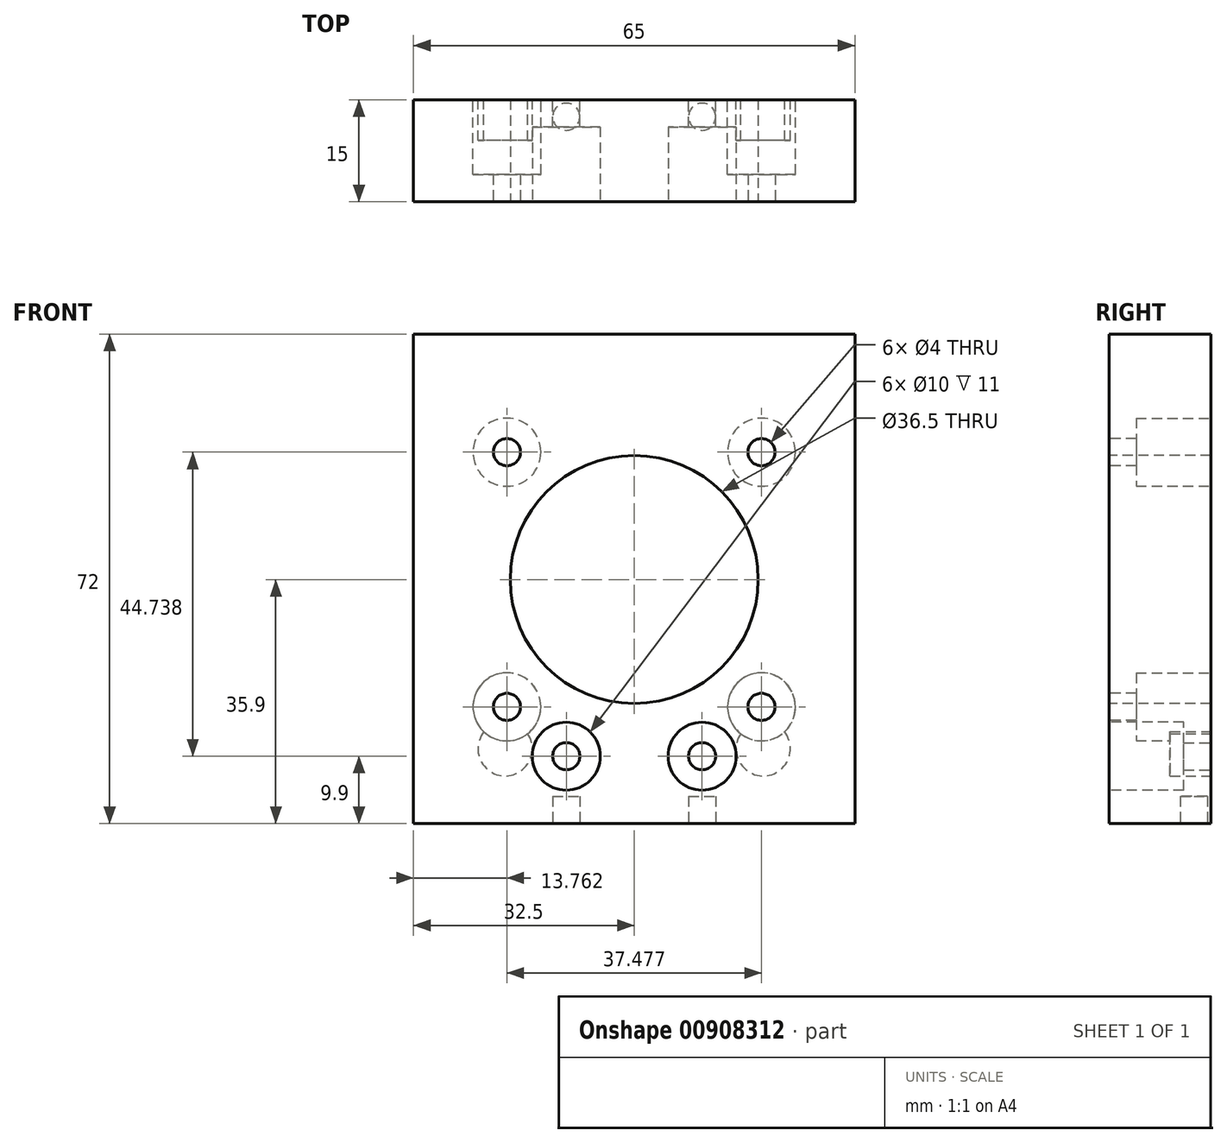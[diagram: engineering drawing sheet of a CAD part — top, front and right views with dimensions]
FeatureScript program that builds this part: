
annotation { "Feature Type Name" : "Feature", "Feature Type Description" : "" }
export const myFeature = defineFeature(function(context is Context, id is Id, definition is map)
    precondition{}
    {
        {
            var Q0;
            Q0=qCreatedBy(makeId("Front.planeOp"),FACE);
            var sketch = newSketch(context, id + "F0", { "sketchPlane" : qUnion([Q0])});
            skLineSegment(sketch, "E0.bottom", {"start": v(32.5, -32.5) * mm, "end": v(-32.5, -32.5) * mm});
            skLineSegment(sketch, "E0.top", {"start": v(32.5, 32.5) * mm, "end": v(-32.5, 32.5) * mm});
            skLineSegment(sketch, "E0.left", {"start": v(32.5, -32.5) * mm, "end": v(32.5, 32.5) * mm});
            skLineSegment(sketch, "E0.right", {"start": v(-32.5, -32.5) * mm, "end": v(-32.5, 32.5) * mm});
            skPoint(sketch, "E0.middle", {"position": v(0, 0) * mm});
            skSolve(sketch);
        }
        {
            var Q0;
            Q0 = qSketchRegion(id + "F0", true);
            extrude(context, id + "F1", {"entities" : qUnion([Q0]), "depth" : 15 * mm, "offsetDistance" : 25 * mm});
        }
        {
            var Q0;
            Q0=makeQuery(id+"F1.opExtrude","CAP_FACE",FACE,{"disambiguationData":[OSD([sQuery(id+"F0.wireOp",EDGE,"E0.bottom"),sQuery(id+"F0.wireOp",EDGE,"E0.top"),sQuery(id+"F0.wireOp",EDGE,"E0.left"),sQuery(id+"F0.wireOp",EDGE,"E0.right")])],"isStart":false});
            var sketch = newSketch(context, id + "F2", { "sketchPlane" : qUnion([Q0])});
            skLineSegment(sketch, "E1", {"start": v(0, -32.5) * mm, "end": v(0, 3.4) * mm});
            skCircle(sketch, "E2", {"center": v(0, 3.4) * mm, "radius": 18.25 * mm});
            skSolve(sketch);
        }
        {
            var Q0;
            Q0=makeQuery(id+"F2.imprint","IMPRINT",FACE,{"disambiguationData":[TD([[makeQuery(id+"F2.imprint","IMPRINT",EDGE,{"derivedFrom":sQuery(id+"F2.wireOp",EDGE,"E2")}),1.0]])]});
            extrude(context, id + "F3", {"entities" : qUnion([Q0]), "operationType" : NewBodyOperationType.REMOVE, "oppositeDirection" : true, "depth" : 15 * mm, "offsetDistance" : 25 * mm});
        }
        {
            var Q0;
            Q0=makeQuery(id+"F1.opExtrude","CAP_FACE",FACE,{"disambiguationData":[OSD([sQuery(id+"F0.wireOp",EDGE,"E0.bottom"),sQuery(id+"F0.wireOp",EDGE,"E0.top"),sQuery(id+"F0.wireOp",EDGE,"E0.left"),sQuery(id+"F0.wireOp",EDGE,"E0.right")])],"isStart":false});
            var sketch = newSketch(context, id + "F4", { "sketchPlane" : qUnion([Q0])});
            skCircle(sketch, "E3", {"center": v(0, 3.4) * mm, "radius": 26.5 * mm});
            skLineSegment(sketch, "E4.bottom", {"start": v(26.5, -23.1) * mm, "end": v(-26.5, -23.1) * mm});
            skLineSegment(sketch, "E4.top", {"start": v(26.5, 29.9) * mm, "end": v(-26.5, 29.9) * mm});
            skLineSegment(sketch, "E4.left", {"start": v(26.5, -23.1) * mm, "end": v(26.5, 29.9) * mm});
            skLineSegment(sketch, "E4.right", {"start": v(-26.5, -23.1) * mm, "end": v(-26.5, 29.9) * mm});
            skLineSegment(sketch, "E5", {"start": v(26.5, 29.9) * mm, "end": v(-26.5, -23.1) * mm});
            skLineSegment(sketch, "E6", {"start": v(26.5, -23.1) * mm, "end": v(-26.5, 29.9) * mm});
            skCircle(sketch, "E7", {"center": v(-18.74, 22.14) * mm, "radius": 2 * mm});
            skCircle(sketch, "E8", {"center": v(18.74, 22.14) * mm, "radius": 2 * mm});
            skCircle(sketch, "E9", {"center": v(-18.74, -15.34) * mm, "radius": 2 * mm});
            skCircle(sketch, "E10", {"center": v(18.74, -15.34) * mm, "radius": 2 * mm});
            skSolve(sketch);
        }
        {
            var Q0;
            {var subQ0=sQuery(id+"F4.wireOp",EDGE,"E6");var subQ1=sQuery(id+"F4.wireOp",EDGE,"E3");var subQ2=makeQuery(id+"F4.imprint","INTERSECT",VERTEX,{"disambiguationData":[OD(0.0)],"derivedFrom":[subQ1,subQ0]});Q0=makeQuery(id+"F4.imprint","IMPRINT",FACE,{"disambiguationData":[TD([[makeQuery(id+"F4.imprint","IMPRINT",EDGE,{"disambiguationData":[TD([[subQ2,-1.0]])],"derivedFrom":subQ1}),-1.0]])]});}
            var Q1;
            {var subQ0=sQuery(id+"F4.wireOp",EDGE,"E8");var subQ1=sQuery(id+"F4.wireOp",EDGE,"E3");var subQ2=makeQuery(id+"F4.imprint","INTERSECT",VERTEX,{"disambiguationData":[OD(0.0)],"derivedFrom":[subQ1,subQ0]});Q1=makeQuery(id+"F4.imprint","IMPRINT",FACE,{"disambiguationData":[TD([[makeQuery(id+"F4.imprint","IMPRINT",EDGE,{"disambiguationData":[TD([[subQ2,-1.0]])],"derivedFrom":subQ1}),-1.0]])]});}
            var Q2;
            {var subQ0=sQuery(id+"F4.wireOp",EDGE,"E5");var subQ1=sQuery(id+"F4.wireOp",EDGE,"E3");var subQ2=makeQuery(id+"F4.imprint","INTERSECT",VERTEX,{"disambiguationData":[OD(0.0)],"derivedFrom":[subQ1,subQ0]});Q2=makeQuery(id+"F4.imprint","IMPRINT",FACE,{"disambiguationData":[TD([[makeQuery(id+"F4.imprint","IMPRINT",EDGE,{"disambiguationData":[TD([[subQ2,-1.0]])],"derivedFrom":subQ1}),1.0]])]});}
            var Q3;
            {var subQ0=sQuery(id+"F4.wireOp",EDGE,"E5");var subQ1=sQuery(id+"F4.wireOp",EDGE,"E3");var subQ2=makeQuery(id+"F4.imprint","INTERSECT",VERTEX,{"disambiguationData":[OD(0.0)],"derivedFrom":[subQ1,subQ0]});Q3=makeQuery(id+"F4.imprint","IMPRINT",FACE,{"disambiguationData":[TD([[makeQuery(id+"F4.imprint","IMPRINT",EDGE,{"disambiguationData":[TD([[subQ2,-1.0]])],"derivedFrom":subQ1}),-1.0]])]});}
            var Q4;
            {var subQ0=sQuery(id+"F4.wireOp",EDGE,"E8");var subQ1=sQuery(id+"F4.wireOp",EDGE,"E3");var subQ2=makeQuery(id+"F4.imprint","INTERSECT",VERTEX,{"disambiguationData":[OD(0.0)],"derivedFrom":[subQ1,subQ0]});Q4=makeQuery(id+"F4.imprint","IMPRINT",FACE,{"disambiguationData":[TD([[makeQuery(id+"F4.imprint","IMPRINT",EDGE,{"disambiguationData":[TD([[subQ2,-1.0]])],"derivedFrom":subQ1}),1.0]])]});}
            var Q5;
            {var subQ0=sQuery(id+"F4.wireOp",EDGE,"E6");var subQ1=sQuery(id+"F4.wireOp",EDGE,"E3");var subQ2=makeQuery(id+"F4.imprint","INTERSECT",VERTEX,{"disambiguationData":[OD(1.0)],"derivedFrom":[subQ1,subQ0]});Q5=makeQuery(id+"F4.imprint","IMPRINT",FACE,{"disambiguationData":[TD([[makeQuery(id+"F4.imprint","IMPRINT",EDGE,{"disambiguationData":[TD([[subQ2,-1.0]])],"derivedFrom":subQ1}),-1.0]])]});}
            var Q6;
            {var subQ0=sQuery(id+"F4.wireOp",EDGE,"E6");var subQ1=sQuery(id+"F4.wireOp",EDGE,"E3");var subQ2=makeQuery(id+"F4.imprint","INTERSECT",VERTEX,{"disambiguationData":[OD(1.0)],"derivedFrom":[subQ1,subQ0]});Q6=makeQuery(id+"F4.imprint","IMPRINT",FACE,{"disambiguationData":[TD([[makeQuery(id+"F4.imprint","IMPRINT",EDGE,{"disambiguationData":[TD([[subQ2,-1.0]])],"derivedFrom":subQ1}),1.0]])]});}
            var Q7;
            {var subQ0=sQuery(id+"F4.wireOp",EDGE,"E10");var subQ1=sQuery(id+"F4.wireOp",EDGE,"E3");var subQ2=makeQuery(id+"F4.imprint","INTERSECT",VERTEX,{"disambiguationData":[OD(0.0)],"derivedFrom":[subQ1,subQ0]});Q7=makeQuery(id+"F4.imprint","IMPRINT",FACE,{"disambiguationData":[TD([[makeQuery(id+"F4.imprint","IMPRINT",EDGE,{"disambiguationData":[TD([[subQ2,-1.0]])],"derivedFrom":subQ1}),-1.0]])]});}
            var Q8;
            {var subQ0=sQuery(id+"F4.wireOp",EDGE,"E10");var subQ1=sQuery(id+"F4.wireOp",EDGE,"E3");var subQ2=makeQuery(id+"F4.imprint","INTERSECT",VERTEX,{"disambiguationData":[OD(0.0)],"derivedFrom":[subQ1,subQ0]});Q8=makeQuery(id+"F4.imprint","IMPRINT",FACE,{"disambiguationData":[TD([[makeQuery(id+"F4.imprint","IMPRINT",EDGE,{"disambiguationData":[TD([[subQ2,-1.0]])],"derivedFrom":subQ1}),1.0]])]});}
            var Q9;
            {var subQ0=sQuery(id+"F4.wireOp",EDGE,"E7");var subQ1=sQuery(id+"F4.wireOp",EDGE,"E3");var subQ2=makeQuery(id+"F4.imprint","INTERSECT",VERTEX,{"disambiguationData":[OD(0.0)],"derivedFrom":[subQ1,subQ0]});Q9=makeQuery(id+"F4.imprint","IMPRINT",FACE,{"disambiguationData":[TD([[makeQuery(id+"F4.imprint","IMPRINT",EDGE,{"disambiguationData":[TD([[subQ2,-1.0]])],"derivedFrom":subQ1}),-1.0]])]});}
            var Q10;
            {var subQ0=sQuery(id+"F4.wireOp",EDGE,"E7");var subQ1=sQuery(id+"F4.wireOp",EDGE,"E3");var subQ2=makeQuery(id+"F4.imprint","INTERSECT",VERTEX,{"disambiguationData":[OD(0.0)],"derivedFrom":[subQ1,subQ0]});Q10=makeQuery(id+"F4.imprint","IMPRINT",FACE,{"disambiguationData":[TD([[makeQuery(id+"F4.imprint","IMPRINT",EDGE,{"disambiguationData":[TD([[subQ2,-1.0]])],"derivedFrom":subQ1}),1.0]])]});}
            var Q11;
            {var subQ0=sQuery(id+"F4.wireOp",EDGE,"E6");var subQ1=sQuery(id+"F4.wireOp",EDGE,"E3");var subQ2=makeQuery(id+"F4.imprint","INTERSECT",VERTEX,{"disambiguationData":[OD(0.0)],"derivedFrom":[subQ1,subQ0]});Q11=makeQuery(id+"F4.imprint","IMPRINT",FACE,{"disambiguationData":[TD([[makeQuery(id+"F4.imprint","IMPRINT",EDGE,{"disambiguationData":[TD([[subQ2,-1.0]])],"derivedFrom":subQ1}),1.0]])]});}
            var Q12;
            {var subQ0=sQuery(id+"F4.wireOp",EDGE,"E5");var subQ1=sQuery(id+"F4.wireOp",EDGE,"E3");var subQ2=makeQuery(id+"F4.imprint","INTERSECT",VERTEX,{"disambiguationData":[OD(1.0)],"derivedFrom":[subQ1,subQ0]});Q12=makeQuery(id+"F4.imprint","IMPRINT",FACE,{"disambiguationData":[TD([[makeQuery(id+"F4.imprint","IMPRINT",EDGE,{"disambiguationData":[TD([[subQ2,-1.0]])],"derivedFrom":subQ1}),1.0]])]});}
            var Q13;
            {var subQ0=sQuery(id+"F4.wireOp",EDGE,"E9");var subQ1=sQuery(id+"F4.wireOp",EDGE,"E3");var subQ2=makeQuery(id+"F4.imprint","INTERSECT",VERTEX,{"disambiguationData":[OD(0.0)],"derivedFrom":[subQ1,subQ0]});Q13=makeQuery(id+"F4.imprint","IMPRINT",FACE,{"disambiguationData":[TD([[makeQuery(id+"F4.imprint","IMPRINT",EDGE,{"disambiguationData":[TD([[subQ2,-1.0]])],"derivedFrom":subQ1}),-1.0]])]});}
            var Q14;
            {var subQ0=sQuery(id+"F4.wireOp",EDGE,"E5");var subQ1=sQuery(id+"F4.wireOp",EDGE,"E3");var subQ2=makeQuery(id+"F4.imprint","INTERSECT",VERTEX,{"disambiguationData":[OD(1.0)],"derivedFrom":[subQ1,subQ0]});Q14=makeQuery(id+"F4.imprint","IMPRINT",FACE,{"disambiguationData":[TD([[makeQuery(id+"F4.imprint","IMPRINT",EDGE,{"disambiguationData":[TD([[subQ2,-1.0]])],"derivedFrom":subQ1}),-1.0]])]});}
            var Q15;
            {var subQ0=sQuery(id+"F4.wireOp",EDGE,"E9");var subQ1=sQuery(id+"F4.wireOp",EDGE,"E3");var subQ2=makeQuery(id+"F4.imprint","INTERSECT",VERTEX,{"disambiguationData":[OD(0.0)],"derivedFrom":[subQ1,subQ0]});Q15=makeQuery(id+"F4.imprint","IMPRINT",FACE,{"disambiguationData":[TD([[makeQuery(id+"F4.imprint","IMPRINT",EDGE,{"disambiguationData":[TD([[subQ2,-1.0]])],"derivedFrom":subQ1}),1.0]])]});}
            extrude(context, id + "F5", {"entities" : qUnion([Q0, Q1, Q2, Q3, Q4, Q5, Q6, Q7, Q8, Q9, Q10, Q11, Q12, Q13, Q14, Q15]), "operationType" : NewBodyOperationType.REMOVE, "oppositeDirection" : true, "depth" : 25 * mm, "offsetDistance" : 25 * mm});
        }
        {
            var Q0;
            Q0=makeQuery(id+"F1.opExtrude","CAP_FACE",FACE,{"disambiguationData":[OSD([sQuery(id+"F0.wireOp",EDGE,"E0.bottom"),sQuery(id+"F0.wireOp",EDGE,"E0.top"),sQuery(id+"F0.wireOp",EDGE,"E0.left"),sQuery(id+"F0.wireOp",EDGE,"E0.right")])],"isStart":true});
            var sketch = newSketch(context, id + "F6", { "sketchPlane" : qUnion([Q0])});
            skCircle(sketch, "E11", {"center": v(-18.74, 22.14) * mm, "radius": 5 * mm});
            skCircle(sketch, "E12", {"center": v(18.74, 22.14) * mm, "radius": 5 * mm});
            skCircle(sketch, "E13", {"center": v(-18.74, -15.34) * mm, "radius": 5 * mm});
            skCircle(sketch, "E14", {"center": v(18.74, -15.34) * mm, "radius": 5 * mm});
            skSolve(sketch);
        }
        {
            var Q0;
            Q0 = qSketchRegion(id + "F6", true);
            extrude(context, id + "F7", {"entities" : qUnion([Q0]), "operationType" : NewBodyOperationType.REMOVE, "oppositeDirection" : true, "depth" : 11 * mm, "offsetDistance" : 25 * mm});
        }
        {
            var Q0;
            Q0=makeQuery(id+"F1.opExtrude","CAP_FACE",FACE,{"disambiguationData":[OSD([sQuery(id+"F0.wireOp",EDGE,"E0.bottom"),sQuery(id+"F0.wireOp",EDGE,"E0.top"),sQuery(id+"F0.wireOp",EDGE,"E0.left"),sQuery(id+"F0.wireOp",EDGE,"E0.right")])],"isStart":true});
            var sketch = newSketch(context, id + "F8", { "sketchPlane" : qUnion([Q0])});
            skLineSegment(sketch, "E15", {"start": v(0, -32.5) * mm, "end": v(0, -22.6) * mm});
            skLineSegment(sketch, "E16", {"start": v(0, -22.6) * mm, "end": v(10, -22.6) * mm});
            skLineSegment(sketch, "E17", {"start": v(10, -22.6) * mm, "end": v(-10, -22.6) * mm});
            skCircle(sketch, "E18", {"center": v(-10, -22.6) * mm, "radius": 2 * mm});
            skCircle(sketch, "E19", {"center": v(10, -22.6) * mm, "radius": 2 * mm});
            skSolve(sketch);
        }
        {
            var Q0;
            Q0 = qSketchRegion(id + "F8", true);
            extrude(context, id + "F9", {"entities" : qUnion([Q0]), "operationType" : NewBodyOperationType.REMOVE, "oppositeDirection" : true, "depth" : 25 * mm, "offsetDistance" : 25 * mm});
        }
        {
            var Q0;
            Q0=makeQuery(id+"F1.opExtrude","CAP_FACE",FACE,{"disambiguationData":[OSD([sQuery(id+"F0.wireOp",EDGE,"E0.bottom"),sQuery(id+"F0.wireOp",EDGE,"E0.top"),sQuery(id+"F0.wireOp",EDGE,"E0.left"),sQuery(id+"F0.wireOp",EDGE,"E0.right")])],"isStart":false});
            var sketch = newSketch(context, id + "F10", { "sketchPlane" : qUnion([Q0])});
            skCircle(sketch, "E20", {"center": v(-10, -22.6) * mm, "radius": 5 * mm});
            skCircle(sketch, "E21", {"center": v(10, -22.6) * mm, "radius": 5 * mm});
            skSolve(sketch);
        }
        {
            var Q0;
            Q0 = qSketchRegion(id + "F10", true);
            extrude(context, id + "F11", {"entities" : qUnion([Q0]), "operationType" : NewBodyOperationType.REMOVE, "oppositeDirection" : true, "depth" : 11 * mm, "offsetDistance" : 25 * mm});
        }
        {
            var Q0;
            Q0=makeQuery(id+"F1.opExtrude","SWEPT_FACE",FACE,{"disambiguationData":[OSD([sQuery(id+"F0.wireOp",EDGE,"E0.bottom")])]});
            var sketch = newSketch(context, id + "F12", { "sketchPlane" : qUnion([Q0])});
            skLineSegment(sketch, "E22", {"start": v(0, 0) * mm, "end": v(-10, 0) * mm});
            skLineSegment(sketch, "E23", {"start": v(-10, 0) * mm, "end": v(-10, 2.5) * mm});
            skLineSegment(sketch, "E24", {"start": v(-10, 2.5) * mm, "end": v(10, 2.5) * mm});
            skCircle(sketch, "E25", {"center": v(-10, 2.5) * mm, "radius": 2 * mm});
            skCircle(sketch, "E26", {"center": v(10, 2.5) * mm, "radius": 2 * mm});
            skSolve(sketch);
        }
        {
            var Q0;
            Q0 = qSketchRegion(id + "F12", true);
            extrude(context, id + "F13", {"entities" : qUnion([Q0]), "operationType" : NewBodyOperationType.REMOVE, "oppositeDirection" : true, "depth" : 4 * mm, "offsetDistance" : 25 * mm});
        }
        {
            var Q0;
            Q0=makeQuery(id+"F1.opExtrude","CAP_FACE",FACE,{"disambiguationData":[OSD([sQuery(id+"F0.wireOp",EDGE,"E0.bottom"),sQuery(id+"F0.wireOp",EDGE,"E0.top"),sQuery(id+"F0.wireOp",EDGE,"E0.left"),sQuery(id+"F0.wireOp",EDGE,"E0.right")])],"isStart":true});
            var sketch = newSketch(context, id + "F14", { "sketchPlane" : qUnion([Q0])});
            skLineSegment(sketch, "E27", {"start": v(0, -32.5) * mm, "end": v(0, -21.5) * mm});
            skLineSegment(sketch, "E28", {"start": v(0, -21.5) * mm, "end": v(-19, -21.5) * mm});
            skLineSegment(sketch, "E29", {"start": v(-19, -21.5) * mm, "end": v(19, -21.5) * mm});
            skCircle(sketch, "E30", {"center": v(-19, -21.5) * mm, "radius": 4 * mm});
            skCircle(sketch, "E31", {"center": v(19, -21.5) * mm, "radius": 4 * mm});
            skSolve(sketch);
        }
        {
            var Q0;
            Q0 = qSketchRegion(id + "F14", true);
            extrude(context, id + "F15", {"entities" : qUnion([Q0]), "operationType" : NewBodyOperationType.REMOVE, "oppositeDirection" : true, "depth" : 6 * mm, "offsetDistance" : 25 * mm});
        }
        {
            var Q0;
            Q0=makeQuery(id+"F1.opExtrude","SWEPT_FACE",FACE,{"disambiguationData":[OSD([sQuery(id+"F0.wireOp",EDGE,"E0.top")])]});
            extrude(context, id + "F16", {"entities" : qUnion([Q0]), "operationType" : NewBodyOperationType.ADD, "depth" : 7 * mm, "offsetDistance" : 25 * mm});
        }
        {
            var Q0;
            Q0=makeQuery(id+"F0.imprint","IMPRINT",FACE,{"disambiguationData":[TD([[makeQuery(id+"F0.imprint","IMPRINT",EDGE,{"derivedFrom":sQuery(id+"F0.wireOp",EDGE,"E0.bottom")}),-1.0]])]});
            var sketch = newSketch(context, id + "F17", { "sketchPlane" : qUnion([Q0])});
            skCircle(sketch, "E32", {"center": v(0, 3.84) * mm, "radius": 24 * mm});
            skLineSegment(sketch, "E33", {"start": v(0, 3.84) * mm, "end": v(0, 39.22) * mm});
            skLineSegment(sketch, "E34", {"start": v(0, 39.22) * mm, "end": v(0, 3.84) * mm});
            skLineSegment(sketch, "E35", {"start": v(24, 3.84) * mm, "end": v(0, 3.84) * mm});
            skLineSegment(sketch, "E36", {"start": v(-24, 4.45) * mm, "end": v(0, 3.84) * mm});
            skCircle(sketch, "E37", {"center": v(0, 27.84) * mm, "radius": 5 * mm});
            skCircle(sketch, "E38", {"center": v(24, 3.84) * mm, "radius": 5 * mm});
            skCircle(sketch, "E39", {"center": v(-24, 4.45) * mm, "radius": 5 * mm});
            skSolve(sketch);
        }
        {
            var Q0;
            Q0=sQuery(id+"F17.wireOp",EDGE,"E37");
            extrude(context, id + "F18", {"bodyType" : ToolBodyType.SURFACE, "surfaceEntities" : qUnion([Q0]), "depth" : 11 * mm, "offsetDistance" : 25 * mm});
        }
    });
